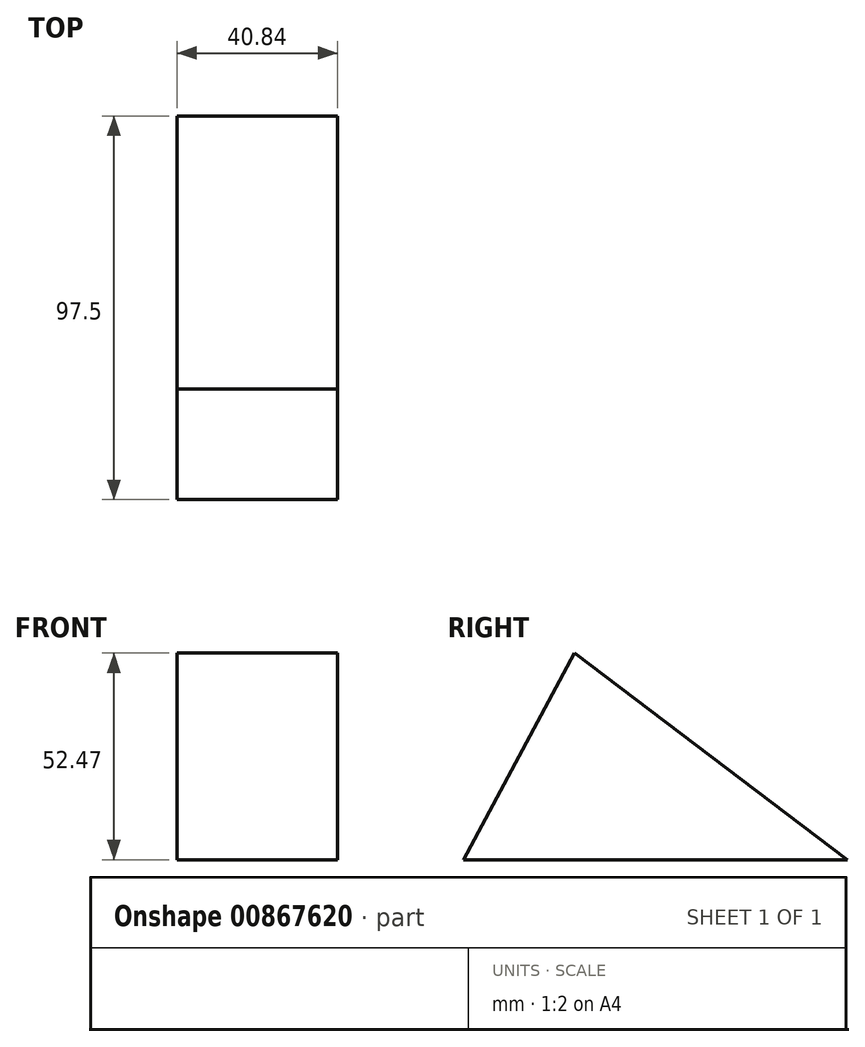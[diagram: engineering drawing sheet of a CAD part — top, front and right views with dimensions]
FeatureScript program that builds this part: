
annotation { "Feature Type Name" : "Feature", "Feature Type Description" : "" }
export const myFeature = defineFeature(function(context is Context, id is Id, definition is map)
    precondition{}
    {
        {
            var Q0;
            Q0=qCreatedBy(makeId("Right.planeOp"),FACE);
            var sketch = newSketch(context, id + "F0", { "sketchPlane" : qUnion([Q0])});
            skLineSegment(sketch, "E0", {"start": v(-28.16, -52.47) * mm, "end": v(0, 0) * mm});
            skLineSegment(sketch, "E1", {"start": v(0, 0) * mm, "end": v(69.34, -52.47) * mm});
            skLineSegment(sketch, "E2", {"start": v(69.34, -52.47) * mm, "end": v(-28.16, -52.47) * mm});
            skSolve(sketch);
        }
        {
            var Q0;
            Q0 = qSketchRegion(id + "F0", true);
            extrude(context, id + "F1", {"entities" : qUnion([Q0]), "depth" : 40.84 * mm, "offsetDistance" : 25.4 * mm});
        }
    });
